# Revit family: Lighting_Ceiling-Mounted_Molto-Luce_Dark-Night-Lens-3-Recessed_999
name_source: partatom
category: Lighting Fixtures
revit_build: Autodesk Revit 2018 (Build: 20170223_1515(x64)
units: mm (PartAtom-declared; Revit-internal decimal feet)

## family parameters
Cut with Voids When Loaded = No
Host = Face
Light Source = Yes
OmniClass Number = 23.80.70.00
OmniClass Title = Lighting
Part Type = Normal
Room Calculation Point = No
Round Connector Dimension = Use Diameter
Shared = No

## types (1)
- Default - please load Revit Family Type Catalog
    BIMobject category = Ceiling Mounted Lighting
    Color Filter = 16777215
    Decor Color = Molto Luce - Gold
    Default Elevation = 1219 mm
    Description = The varied product family DARK NIGHT impresses with its adaptability, as a downlight, swiveling downlight, pendant luminaire with
canopy or VOLARE adapter to a surface mounted downlight, DARK NIGHT can do it all. DARK NIGHT LGP is a special highlight, which
impresses with the option of emitting either directed direct light or diffuse light via the Light Guide Pipe. The possibility of mixing
diffuse and directed light opens up completely new possibilities to stage rooms differently. The DARK NIGHT family is available in black
and white powder-coated housings and reflectors in high-gloss black, matt silver, white and gold.
Design: INHOUSE
    Design country = Austria
    Dimming Lamp Color Temperature Shift = <None>
    Edition number = 1
    Housing Color = Molto Luce - Black
    IFC Classification = Lamp
    Light Source Symbol Length = 3048 mm  [stored 10 ft]
    Manufacturer = Molto Luce
    Manufacturer country = Austria
    Manufacturer name = Molto Luce
    Masterformat 2014 Code = 26 50 00
    Masterformat 2014 Description = Lighting
    Material main = Aluminium
    Model = Dark-Night Lens 3 Recessed
    NBS Reference Code = 49
    NBS Reference Description = Luminaires And Lamps
    OmniClass Code = 23-35 45 15
    OmniClass Description = Lamps
    Product Guid = 32f1f60a-ae46-4841-8787-20cf4d2d9b8a
    Product SKU = Dark_Night_Lens_3_Recessed
    Product data url = https://bimobject.com
    Product family = Lighting
    Product group = Recessed Luminaire
    Product name = Dark-Night Lens 3 Recessed
    QR code = https://bimobject.com
    Spot Beam Angle = 70.00°
    Spot Field Angle = 70.00°
    Tilt Angle = 60.00°
    UNSPSC Code = 3911
    URL = https://www.moltoluce.com
    Uniclass 1.4 Code = JY73
    Uniclass 1.4 Description = Luminaires and lamps
    Uniclass 2.0 Code = PR-49
    Uniclass 2.0 Description = Luminaires And Lamps
    Uniclass 2015 Code = Pr_70_70_48
    Uniclass 2015 Name = Luminaires, lighting track and lighting accessories
    Uniformat II Code = D5020
    Uniformat II Description = Lighting & Branch Wiring

note: [stored X ft] marks values corroborated as IEEE doubles in the binary element streams (Revit-internal decimal feet)

## geometry (parser evidence)
native form markers: Sweep x3
no freeform markers — native parametric forms only
